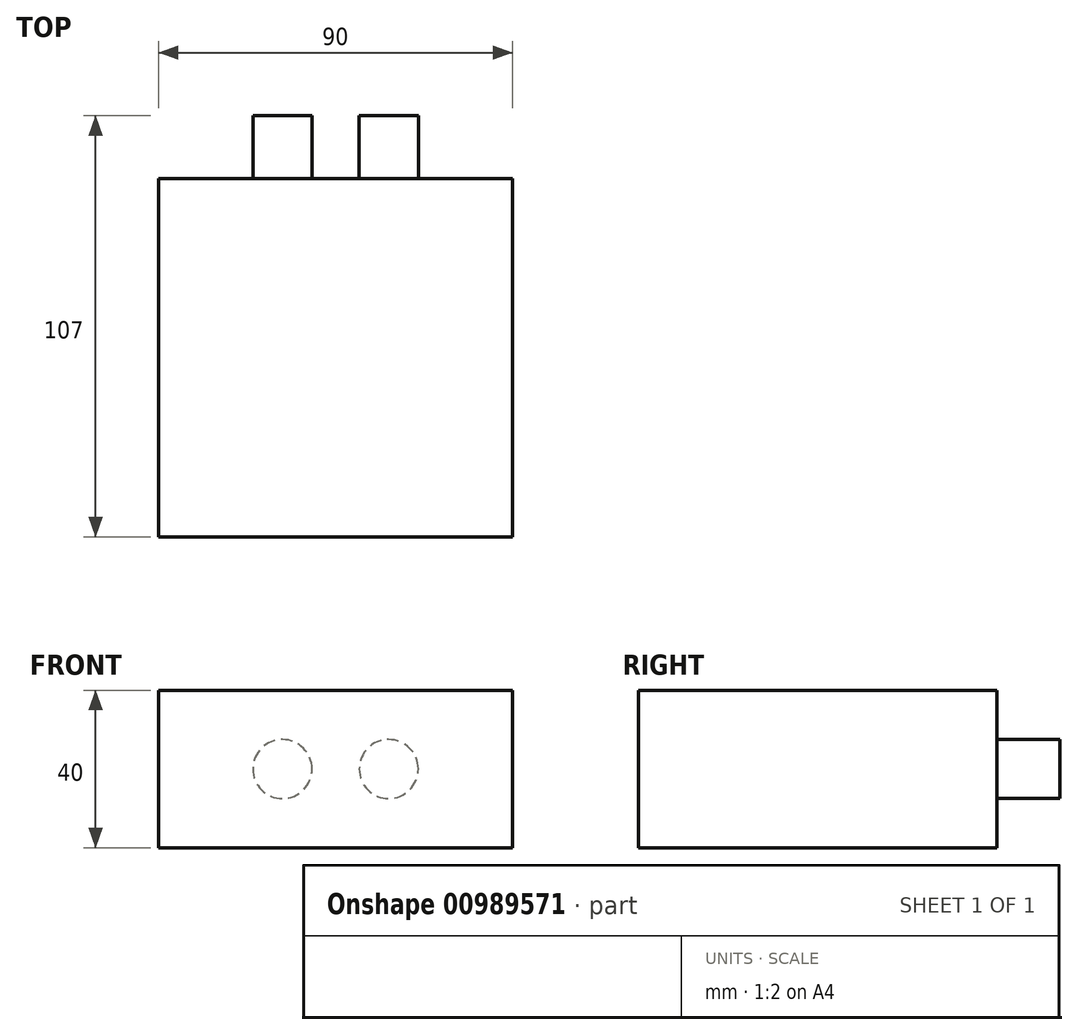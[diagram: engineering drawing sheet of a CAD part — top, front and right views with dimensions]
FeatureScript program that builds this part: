
annotation { "Feature Type Name" : "Feature", "Feature Type Description" : "" }
export const myFeature = defineFeature(function(context is Context, id is Id, definition is map)
    precondition{}
    {
        {
            var Q0;
            Q0=qCreatedBy(makeId("Front.planeOp"),FACE);
            var sketch = newSketch(context, id + "F0", { "sketchPlane" : qUnion([Q0])});
            skCircle(sketch, "E0", {"center": v(-13.5, 0) * mm, "radius": 7.5 * mm});
            skCircle(sketch, "E1", {"center": v(13.5, 0) * mm, "radius": 7.5 * mm});
            skSolve(sketch);
        }
        {
            var Q0;
            Q0 = qSketchRegion(id + "F0", true);
            extrude(context, id + "F1", {"entities" : qUnion([Q0]), "depth" : 16 * mm, "offsetDistance" : 25 * mm});
        }
        {
            var Q0;
            Q0=makeQuery(id+"F1.opExtrude","CAP_FACE",FACE,{"disambiguationData":[OSD([sQuery(id+"F0.wireOp",EDGE,"E0")])],"isStart":false});
            var sketch = newSketch(context, id + "F2", { "sketchPlane" : qUnion([Q0])});
            skLineSegment(sketch, "E2.bottom", {"start": v(-45, 20) * mm, "end": v(45, 20) * mm});
            skLineSegment(sketch, "E2.top", {"start": v(-45, -20) * mm, "end": v(45, -20) * mm});
            skLineSegment(sketch, "E2.left", {"start": v(-45, 20) * mm, "end": v(-45, -20) * mm});
            skLineSegment(sketch, "E2.right", {"start": v(45, 20) * mm, "end": v(45, -20) * mm});
            skSolve(sketch);
        }
        {
            var Q0;
            Q0 = qSketchRegion(id + "F2", true);
            extrude(context, id + "F3", {"entities" : qUnion([Q0]), "depth" : 91 * mm, "offsetDistance" : 25 * mm});
        }
    });
